# Revit family: IS_Tesi_A6565_BIM_FR
name_source: partatom
category: Plumbing Fixtures
revit_build: Autodesk Revit 2017 (Build: 20160225_1515(x64)
units: mm (PartAtom-declared; Revit-internal decimal feet)

## family parameters
Always vertical = Yes
Cut with Voids When Loaded = No
OmniClass Number = 23.45.55.17
OmniClass Title = Mixing Faucets
Part Type = Normal
Room Calculation Point = No
Round Connector Dimension = Use Diameter
Shared = No
Work Plane-Based = No

## types (1)
- A6565AA - TESI BSN MXR RMTD CHR GRANDE CH3
    Accessoires = www.idealspec.fr
    Auteur = Ideal Standard
    BOSUseNativeGeometries = 1
    Bim-NomDuProjet = ISI_IdealStandard_WashbasinTaps_Tesi_A6565
    Caractéristiques = TESI Mitigeur lavabo monotrou
    CodeBarre = 4015413338295
    Conformité = NF
    ConseilsDInstallation = 0
    Cost = 0 $
    Couleur = Chrome
    CoûtDeRemplacement = 0
    DateDeCréation = 2018_08_03
    Description = TESI Mitigeur lavabo monotrou
    Dimensions = 50 x 171 x 212 mm
    EAN code = https://4015413338295
    Espace = Interne
    Finition = Chrome
    Forme = sculpté
    Hauteur = 212 mm
    IfcExportAs = Washbasin taps
    IfcExportType = IfcValveType
    InformationsProduit = www.idealspec.fr
    Largeur = 50 mm  [stored 0.164042 ft]
    Longueur = 171 mm
    Marque = Ideal Standard
    Matériel = Brass
    Model = A6565AA
    Nom = WashbasinTaps_Tesi_A6565_IdealStandard
    PoidsNet = 1,52 KG
    Profondeur = 0 mm  [stored 0 ft]
    Raccordement = Plomberie
    Révision = 1
    TestDePression = 0
    URL = www.idealspec.fr
    Uniclass2015Code = Pr_40_20_87_98
    Uniclass2015Title = Washbasin taps
    Uniclass2015Version = Products v1.1
    UnitéDeMesure = Millimètres
    UnitéDeTemps = An
    UnitéMonétaire = €
    UrlDuFabricant = www.idealspec.fr
    Version = 1

note: [stored X ft] marks values corroborated as IEEE doubles in the binary element streams (Revit-internal decimal feet)

## geometry (parser evidence)
native form markers: Sweep x3
no freeform markers — native parametric forms only
